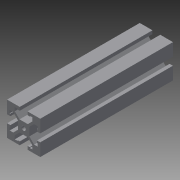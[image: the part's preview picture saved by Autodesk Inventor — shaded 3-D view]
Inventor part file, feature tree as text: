
AUTODESK INVENTOR PART (.ipt)
format: ipt  version: 2014 (Build 180170000, 170)  size: 143,872 bytes
history: native  units: in
note: dims shown in document units (in); Inventor stores cm internally (conversion verified against a paired STEP export)
features: extrude x2, sketch x2, pattern_circular x1
ambient origin geometry x8: Origin, YZ Plane, XZ Plane, XY Plane, X Axis, Y Axis, Z Axis, Center Point
bodies: Solid1 (feature_tree)
feature tree (5):
  extrude  "Extrusion1"  Depth=0.515in
  extrude  "Extrusion2"  TaperAngle=45.0deg  [1 undecoded]
  pattern_circular  "Circular Pattern1"  [2 undecoded]
  sketch  "Sketch1"  dims[d0=0.515in d1=0.19in]
  sketch  "Sketch2"  dims[d2=6.0in d3=0.0in d5=45.0deg d6=0.575in d7=0.15in d8=0.12in d9=0.75in d10=0.75in d13=0.35in d14=0.05in d15=0.125in d16=1.0in d17=0.0in d18=1.5748in d19=360.0deg]
note: 3 required parameter values undecoded (feature->parameter linkage not recoverable at this tier; creation-order binding heuristic only, values carry confidence <= 0.55)
